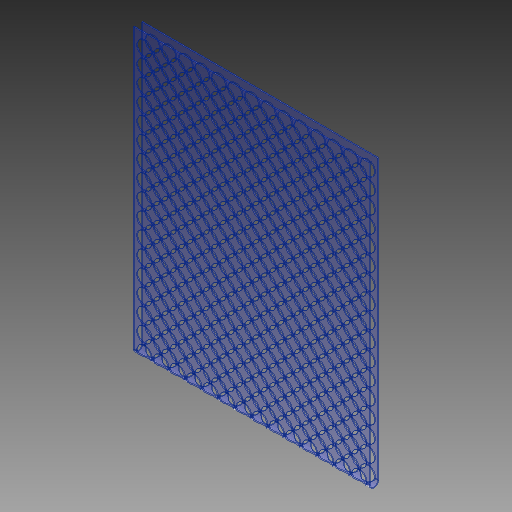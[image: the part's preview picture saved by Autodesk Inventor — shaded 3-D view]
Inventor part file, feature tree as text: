
AUTODESK INVENTOR PART (.ipt)
format: ipt  version: 2018.1 (Build 221171000, 171)  size: 1,449,984 bytes
history: native  units: mm
features: sketch x3, other x2, extrude x2
ambient origin geometry x8: Origin, YZ Plane, XZ Plane, XY Plane, X Axis, Y Axis, Z Axis, Center Point
bodies: Solid1 (feature_tree)
feature tree (7):
  parser-record x1  (decoder bookkeeping rows leaked as tree rows — omitted from the tree; the rows remain in map.json)
  extrude  "Extrusion1"  Depth=624.0mm
  extrude  "Extrusion2"  TaperAngle=0.0deg  [1 undecoded]
  other  "Bend Part1"
  sketch  "Sketch1"  dims[d0=257.0mm d1=624.0mm]
  sketch  "Sketch2"  dims[d2=1.0mm d3=0.0mm]
  sketch  "Sketch3"  dims[d4=16.0mm d5=16.0mm d6=7.0mm d7=3.5mm d8=16.0mm d9=8.0mm d10=8.0mm d11=340.0mm d13=18.0mm d14=140.0mm d16=18.0mm d19=1.0mm d20=0.0mm d21=5.0mm d22=180.0deg d23=312.0mm d24=312.0mm d25=15.0mm d26=15.0mm d27=11.5mm d28=11.5mm]
note: 1 required parameter value undecoded (feature->parameter linkage not recoverable at this tier; creation-order binding heuristic only, values carry confidence <= 0.55)
note: 1 file-system path scrubbed to <path> (originals preserved in map.json)
